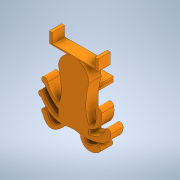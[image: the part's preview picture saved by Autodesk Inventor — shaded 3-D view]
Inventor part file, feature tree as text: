
AUTODESK INVENTOR PART (.ipt)
format: ipt  version: 2020 (Build 240168000, 168)  size: 243,712 bytes
history: native  units: mm
features: extrude x4, sketch x4
ambient origin geometry x8: Origin, YZ Plane, XZ Plane, XY Plane, X Axis, Y Axis, Z Axis, Center Point
bodies: Solid1 (feature_tree)
feature tree (8):
  extrude  "Extrusion1"  Depth=25.0mm
  extrude  "Belt box"  Depth=5.0mm
  extrude  "belt cut out"  Depth=5.0mm
  extrude  "Extrusion4"  Depth=10.0mm
  sketch  "Sketch2"  dims[d6=40.0mm d7=25.0mm]
  sketch  "Sketch3"  dims[d8=5.0mm d9=5.0mm]
  sketch  "Sketch4"  dims[d10=5.0mm d11=5.0mm]
  sketch  "Sketch5"  dims[d12=5.0mm d13=5.0mm d14=10.0mm d15=0.0mm d16=15.0mm d17=20.0mm d18=15.0mm d19=0.0mm d20=8.0mm d21=8.0mm d22=15.0mm d23=0.7mm d24=15.0mm d25=27.5mm d26=15.0mm d27=0.0mm d29=1.0mm d30=25.0mm d31=25.0mm d33=8.0mm d34=8.0mm d36=10.0mm d37=0.0mm]
